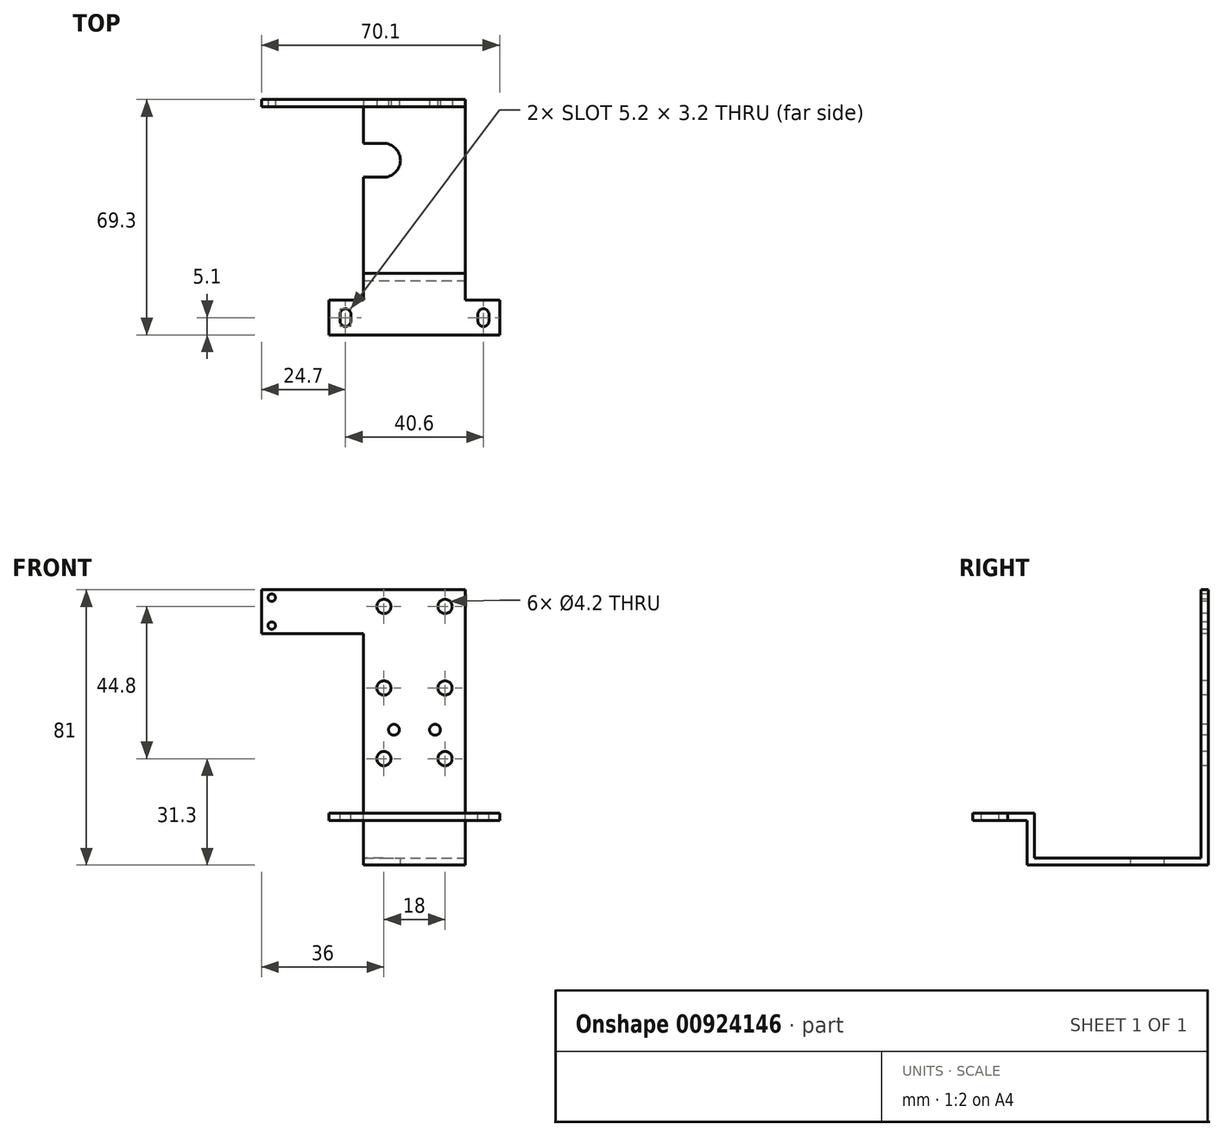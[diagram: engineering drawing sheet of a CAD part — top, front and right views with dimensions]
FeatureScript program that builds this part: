
annotation { "Feature Type Name" : "Feature", "Feature Type Description" : "" }
export const myFeature = defineFeature(function(context is Context, id is Id, definition is map)
    precondition{}
    {
        {
            var Q0;
            Q0=qCreatedBy(makeId("Front.planeOp"),FACE);
            var sketch = newSketch(context, id + "F0", { "sketchPlane" : qUnion([Q0])});
            skLineSegment(sketch, "E0.bottom", {"start": v(15, -40.5) * mm, "end": v(-15, -40.5) * mm});
            skLineSegment(sketch, "E0.top", {"start": v(15, 40.5) * mm, "end": v(-15, 40.5) * mm});
            skLineSegment(sketch, "E0.left", {"start": v(15, -40.5) * mm, "end": v(15, 40.5) * mm});
            skLineSegment(sketch, "E0.right", {"start": v(-15, -40.5) * mm, "end": v(-15, 40.5) * mm});
            skPoint(sketch, "E0.middle", {"position": v(0, 0) * mm});
            skSolve(sketch);
        }
        {
            var Q0;
            Q0=qSketchRegion(id+"F0",true);
            extrude(context, id + "F1", {"entities" : qUnion([Q0]), "offsetDistance" : 25 * mm, "depth" : 2.1 * mm});
        }
        {
            var Q0;
            Q0=makeQuery(id+"F1.opExtrude","CAP_FACE",FACE,{"disambiguationData":[OSD([sQuery(id+"F0.wireOp",EDGE,"E0.bottom"),sQuery(id+"F0.wireOp",EDGE,"E0.top"),sQuery(id+"F0.wireOp",EDGE,"E0.left"),sQuery(id+"F0.wireOp",EDGE,"E0.right")])],"isStart":false});
            var sketch = newSketch(context, id + "F2", { "sketchPlane" : qUnion([Q0])});
            skLineSegment(sketch, "E1.bottom", {"start": v(-15, -40.5) * mm, "end": v(15, -40.5) * mm});
            skLineSegment(sketch, "E1.top", {"start": v(-15, -38.4) * mm, "end": v(15, -38.4) * mm});
            skLineSegment(sketch, "E1.left", {"start": v(-15, -40.5) * mm, "end": v(-15, -38.4) * mm});
            skLineSegment(sketch, "E1.right", {"start": v(15, -40.5) * mm, "end": v(15, -38.4) * mm});
            skSolve(sketch);
        }
        {
            var Q0;
            Q0=qSketchRegion(id+"F2",true);
            extrude(context, id + "F3", {"entities" : qUnion([Q0]), "operationType" : NewBodyOperationType.ADD, "depth" : 51.2 * mm});
        }
        {
            var Q0;
            Q0=makeQuery(id+"F3.opExtrude","SWEPT_FACE",FACE,{"disambiguationData":[OSD([sQuery(id+"F2.wireOp",EDGE,"E1.top")])]});
            var sketch = newSketch(context, id + "F4", { "sketchPlane" : qUnion([Q0])});
            skLineSegment(sketch, "E2.bottom", {"start": v(-15, -53.3) * mm, "end": v(15, -53.3) * mm});
            skLineSegment(sketch, "E2.top", {"start": v(-15, -51.2) * mm, "end": v(15, -51.2) * mm});
            skLineSegment(sketch, "E2.left", {"start": v(-15, -53.3) * mm, "end": v(-15, -51.2) * mm});
            skLineSegment(sketch, "E2.right", {"start": v(15, -53.3) * mm, "end": v(15, -51.2) * mm});
            skSolve(sketch);
        }
        {
            var Q0;
            Q0=qSketchRegion(id+"F4",true);
            extrude(context, id + "F5", {"entities" : qUnion([Q0]), "operationType" : NewBodyOperationType.ADD, "depth" : 13.1 * mm});
        }
        {
            var Q0;
            Q0=makeQuery(id+"F5.boolean.opBoolean","MERGE",FACE,{"derivedFrom":[makeQuery(id+"F3.opExtrude","CAP_FACE",FACE,{"disambiguationData":[OSD([sQuery(id+"F2.wireOp",EDGE,"E1.bottom"),sQuery(id+"F2.wireOp",EDGE,"E1.top"),sQuery(id+"F2.wireOp",EDGE,"E1.left"),sQuery(id+"F2.wireOp",EDGE,"E1.right")])],"isStart":false}),makeQuery(id+"F5.opExtrude","SWEPT_FACE",FACE,{"disambiguationData":[OSD([sQuery(id+"F4.wireOp",EDGE,"E2.bottom")])]})]});
            var sketch = newSketch(context, id + "F6", { "sketchPlane" : qUnion([Q0])});
            skLineSegment(sketch, "E3.bottom", {"start": v(-15, -25.3) * mm, "end": v(15, -25.3) * mm});
            skLineSegment(sketch, "E3.top", {"start": v(-15, -27.4) * mm, "end": v(15, -27.4) * mm});
            skLineSegment(sketch, "E3.left", {"start": v(-15, -25.3) * mm, "end": v(-15, -27.4) * mm});
            skLineSegment(sketch, "E3.right", {"start": v(15, -25.3) * mm, "end": v(15, -27.4) * mm});
            skSolve(sketch);
        }
        {
            var Q0;
            Q0=qSketchRegion(id+"F6",true);
            extrude(context, id + "F7", {"entities" : qUnion([Q0]), "operationType" : NewBodyOperationType.ADD, "depth" : 16 * mm});
        }
        {
            var Q0;
            Q0=makeQuery(id+"F7.boolean.opBoolean","MERGE",FACE,{"derivedFrom":[makeQuery(id+"F5.opExtrude","CAP_FACE",FACE,{"disambiguationData":[OSD([sQuery(id+"F4.wireOp",EDGE,"E2.bottom"),sQuery(id+"F4.wireOp",EDGE,"E2.top"),sQuery(id+"F4.wireOp",EDGE,"E2.left"),sQuery(id+"F4.wireOp",EDGE,"E2.right")])],"isStart":false}),makeQuery(id+"F7.opExtrude","SWEPT_FACE",FACE,{"disambiguationData":[OSD([sQuery(id+"F6.wireOp",EDGE,"E3.bottom")])]})]});
            var sketch = newSketch(context, id + "F8", { "sketchPlane" : qUnion([Q0])});
            skLineSegment(sketch, "E4.bottom", {"start": v(-25.1, -69.3) * mm, "end": v(25.1, -69.3) * mm});
            skLineSegment(sketch, "E4.top", {"start": v(-25.1, -59.1) * mm, "end": v(25.1, -59.1) * mm});
            skLineSegment(sketch, "E4.left", {"start": v(-25.1, -69.3) * mm, "end": v(-25.1, -59.1) * mm});
            skLineSegment(sketch, "E4.right", {"start": v(25.1, -69.3) * mm, "end": v(25.1, -59.1) * mm});
            skLineSegment(sketch, "E5", {"start": v(0, -51.2) * mm, "end": v(0, -65.26) * mm});
            skSolve(sketch);
        }
        {
            var Q0;
            {var subQ3=sQuery(id+"F8.wireOp",EDGE,"E4.left");Q0=makeQuery(id+"F8.imprint","IMPRINT",FACE,{"disambiguationData":[TD([[makeQuery(id+"F8.imprint","IMPRINT",EDGE,{"derivedFrom":subQ3}),-1.0]])]});}
            var Q1;
            {var subQ3=sQuery(id+"F8.wireOp",EDGE,"E4.right");Q1=makeQuery(id+"F8.imprint","IMPRINT",FACE,{"disambiguationData":[TD([[makeQuery(id+"F8.imprint","IMPRINT",EDGE,{"derivedFrom":subQ3}),1.0]])]});}
            extrude(context, id + "F9", {"entities" : qUnion([Q0, Q1]), "operationType" : NewBodyOperationType.ADD, "oppositeDirection" : true, "depth" : 2.1 * mm});
        }
        {
            var Q0;
            {var subQ0=sQuery(id+"F8.wireOp",EDGE,"E4.top");var subQ1=sQuery(id+"F8.wireOp",EDGE,"E4.bottom");var subQ2=sQuery(id+"F6.wireOp",EDGE,"E3.bottom");var subQ3=sQuery(id+"F4.wireOp",EDGE,"E2.right");var subQ4=sQuery(id+"F4.wireOp",EDGE,"E2.left");Q0=makeQuery(id+"F9.boolean.opBoolean","MERGE",FACE,{"derivedFrom":[makeQuery(id+"F7.boolean.opBoolean","MERGE",FACE,{"derivedFrom":[makeQuery(id+"F5.opExtrude","CAP_FACE",FACE,{"disambiguationData":[OSD([sQuery(id+"F4.wireOp",EDGE,"E2.bottom"),sQuery(id+"F4.wireOp",EDGE,"E2.top"),subQ4,subQ3])],"isStart":false}),makeQuery(id+"F7.opExtrude","SWEPT_FACE",FACE,{"disambiguationData":[OSD([subQ2])]})]}),makeQuery(id+"F9.opExtrude","CAP_FACE",FACE,{"disambiguationData":[OSD([subQ4,subQ2,sQuery(id+"F6.wireOp",EDGE,"E3.left"),subQ1,subQ0,sQuery(id+"F8.wireOp",EDGE,"E4.left")])],"isStart":true}),makeQuery(id+"F9.opExtrude","CAP_FACE",FACE,{"disambiguationData":[OSD([subQ3,subQ2,sQuery(id+"F6.wireOp",EDGE,"E3.right"),subQ1,subQ0,sQuery(id+"F8.wireOp",EDGE,"E4.right")])],"isStart":true})]});}
            var sketch = newSketch(context, id + "F10", { "sketchPlane" : qUnion([Q0])});
            skArc(sketch, "E6", {"start": v(-21.9, -65.2) * mm, "mid": v(-20.3, -66.8) * mm, "end": v(-18.7, -65.2) * mm});
            skArc(sketch, "E7", {"start": v(-18.7, -63.2) * mm, "mid": v(-20.3, -61.6) * mm, "end": v(-21.9, -63.2) * mm});
            skLineSegment(sketch, "E8", {"start": v(-21.9, -63.2) * mm, "end": v(-21.9, -65.2) * mm});
            skLineSegment(sketch, "E9", {"start": v(-18.7, -65.2) * mm, "end": v(-18.7, -63.2) * mm});
            skLineSegment(sketch, "E10", {"start": v(-20.3, -63.2) * mm, "end": v(-20.3, -65.2) * mm});
            skPoint(sketch, "E11", {"position": v(-20.3, -64.2) * mm});
            skLineSegment(sketch, "E12", {"start": v(0, -69.3) * mm, "end": v(0, -51.2) * mm});
            skLineSegment(sketch, "E13.MirrorCS", {"start": v(18.7, -65.2) * mm, "end": v(18.7, -63.2) * mm});
            skArc(sketch, "E14.MirrorCS", {"start": v(18.7, -63.2) * mm, "mid": v(20.3, -61.6) * mm, "end": v(21.9, -63.2) * mm});
            skLineSegment(sketch, "E15.MirrorCS", {"start": v(21.9, -63.2) * mm, "end": v(21.9, -65.2) * mm});
            skArc(sketch, "E16.MirrorCS", {"start": v(21.9, -65.2) * mm, "mid": v(20.3, -66.8) * mm, "end": v(18.7, -65.2) * mm});
            skSolve(sketch);
        }
        {
            var Q0;
            Q0=makeQuery(id+"F10.imprint","IMPRINT",FACE,{"disambiguationData":[TD([[makeQuery(id+"F10.imprint","IMPRINT",EDGE,{"derivedFrom":sQuery(id+"F10.wireOp",EDGE,"E6")}),1.0]])]});
            var Q1;
            Q1=makeQuery(id+"F10.imprint","IMPRINT",FACE,{"disambiguationData":[TD([[makeQuery(id+"F10.imprint","IMPRINT",EDGE,{"derivedFrom":sQuery(id+"F10.wireOp",EDGE,"E13.MirrorCS")}),-1.0]])]});
            extrude(context, id + "F11", {"entities" : qUnion([Q0, Q1]), "operationType" : NewBodyOperationType.REMOVE, "endBound" : BoundingType.THROUGH_ALL, "oppositeDirection" : true, "depth" : 25 * mm});
        }
        {
            var Q0;
            Q0=makeQuery(id+"F3.opExtrude","SWEPT_FACE",FACE,{"disambiguationData":[OSD([sQuery(id+"F2.wireOp",EDGE,"E1.top")])]});
            var sketch = newSketch(context, id + "F12", { "sketchPlane" : qUnion([Q0])});
            skArc(sketch, "E17", {"start": v(-9.15, -22.9) * mm, "mid": v(-4.15, -17.9) * mm, "end": v(-9.15, -12.9) * mm});
            skLineSegment(sketch, "E18", {"start": v(-9.15, -12.9) * mm, "end": v(-15, -12.9) * mm});
            skLineSegment(sketch, "E19", {"start": v(-9.15, -22.9) * mm, "end": v(-15, -22.9) * mm});
            skLineSegment(sketch, "E20", {"start": v(-15, -22.9) * mm, "end": v(-15, -12.9) * mm});
            skSolve(sketch);
        }
        {
            var Q0;
            Q0=qSketchRegion(id+"F12",true);
            extrude(context, id + "F13", {"entities" : qUnion([Q0]), "operationType" : NewBodyOperationType.REMOVE, "endBound" : BoundingType.THROUGH_ALL, "oppositeDirection" : true, "depth" : 25 * mm});
        }
        {
            var Q0;
            Q0=makeQuery(id+"F1.opExtrude","CAP_FACE",FACE,{"disambiguationData":[OSD([sQuery(id+"F0.wireOp",EDGE,"E0.bottom"),sQuery(id+"F0.wireOp",EDGE,"E0.top"),sQuery(id+"F0.wireOp",EDGE,"E0.left"),sQuery(id+"F0.wireOp",EDGE,"E0.right")])],"isStart":false});
            var sketch = newSketch(context, id + "F14", { "sketchPlane" : qUnion([Q0])});
            skCircle(sketch, "E21", {"center": v(9, 35.6) * mm, "radius": 2.1 * mm});
            skCircle(sketch, "E22.0.1.0", {"center": v(9, 11.6) * mm, "radius": 2.1 * mm});
            skCircle(sketch, "E22.1.0.0", {"center": v(-9, 35.6) * mm, "radius": 2.1 * mm});
            skCircle(sketch, "E22.1.1.0", {"center": v(-9, 11.6) * mm, "radius": 2.1 * mm});
            skLineSegment(sketch, "E22.direction1", {"start": v(9, 35.6) * mm, "end": v(-9, 35.6) * mm, "construction": true});
            skLineSegment(sketch, "E22.direction2", {"start": v(9, 35.6) * mm, "end": v(9, 11.6) * mm, "construction": true});
            skCircle(sketch, "E23", {"center": v(9, -9.2) * mm, "radius": 2.1 * mm});
            skCircle(sketch, "E24.1.0.0", {"center": v(-9, -9.2) * mm, "radius": 2.1 * mm});
            skLineSegment(sketch, "E24.direction1", {"start": v(9, -9.2) * mm, "end": v(-9, -9.2) * mm, "construction": true});
            skCircle(sketch, "E25", {"center": v(6.05, -0.7) * mm, "radius": 1.6 * mm});
            skCircle(sketch, "E26", {"center": v(-6.05, -0.7) * mm, "radius": 1.6 * mm});
            skSolve(sketch);
        }
        {
            var Q0;
            Q0=qSketchRegion(id+"F14",true);
            extrude(context, id + "F15", {"entities" : qUnion([Q0]), "operationType" : NewBodyOperationType.REMOVE, "endBound" : BoundingType.THROUGH_ALL, "oppositeDirection" : true, "depth" : 25 * mm});
        }
        {
            var Q0;
            {var subQ0=sQuery(id+"F0.wireOp",EDGE,"E0.top");var subQ1=sQuery(id+"F0.wireOp",EDGE,"E0.right");Q0=makeQuery(id+"F13.boolean.opBoolean","SPLIT",FACE,{"disambiguationData":[TD([makeQuery(id+"F1.opExtrude","SWEPT_FACE",FACE,{"disambiguationData":[OSD([subQ0])]})])],"derivedFrom":makeQuery(id+"F7.boolean.opBoolean","MERGE",FACE,{"derivedFrom":[makeQuery(id+"F5.boolean.opBoolean","MERGE",FACE,{"derivedFrom":[makeQuery(id+"F3.boolean.opBoolean","MERGE",FACE,{"derivedFrom":[makeQuery(id+"F1.opExtrude","SWEPT_FACE",FACE,{"disambiguationData":[OSD([subQ1])]}),makeQuery(id+"F3.opExtrude","SWEPT_FACE",FACE,{"disambiguationData":[OSD([sQuery(id+"F2.wireOp",EDGE,"E1.left")])]})]}),makeQuery(id+"F5.opExtrude","SWEPT_FACE",FACE,{"disambiguationData":[OSD([sQuery(id+"F4.wireOp",EDGE,"E2.left")])]})]}),makeQuery(id+"F7.opExtrude","SWEPT_FACE",FACE,{"disambiguationData":[OSD([sQuery(id+"F6.wireOp",EDGE,"E3.left")])]})]})});}
            var sketch = newSketch(context, id + "F16", { "sketchPlane" : qUnion([Q0])});
            skLineSegment(sketch, "E27.bottom", {"start": v(0, 40.5) * mm, "end": v(2.1, 40.5) * mm});
            skLineSegment(sketch, "E27.top", {"start": v(0, 27.65) * mm, "end": v(2.1, 27.65) * mm});
            skLineSegment(sketch, "E27.left", {"start": v(0, 40.5) * mm, "end": v(0, 27.65) * mm});
            skLineSegment(sketch, "E27.right", {"start": v(2.1, 40.5) * mm, "end": v(2.1, 27.65) * mm});
            skSolve(sketch);
        }
        {
            var Q0;
            Q0=qSketchRegion(id+"F16",true);
            extrude(context, id + "F17", {"entities" : qUnion([Q0]), "operationType" : NewBodyOperationType.ADD, "depth" : 30 * mm, "offsetDistance" : 25 * mm});
        }
        {
            var Q0;
            Q0=makeQuery(id+"F17.boolean.opBoolean","MERGE",FACE,{"derivedFrom":[makeQuery(id+"F1.opExtrude","CAP_FACE",FACE,{"disambiguationData":[OSD([sQuery(id+"F0.wireOp",EDGE,"E0.bottom"),sQuery(id+"F0.wireOp",EDGE,"E0.top"),sQuery(id+"F0.wireOp",EDGE,"E0.left"),sQuery(id+"F0.wireOp",EDGE,"E0.right")])],"isStart":false}),makeQuery(id+"F17.opExtrude","SWEPT_FACE",FACE,{"disambiguationData":[OSD([sQuery(id+"F16.wireOp",EDGE,"E27.right")])]})]});
            var sketch = newSketch(context, id + "F18", { "sketchPlane" : qUnion([Q0])});
            skCircle(sketch, "E28", {"center": v(-42, 38.17) * mm, "radius": 1.1 * mm});
            skCircle(sketch, "E29", {"center": v(-42, 29.97) * mm, "radius": 1.1 * mm});
            skLineSegment(sketch, "E30", {"start": v(-45, 34.08) * mm, "end": v(-26.44, 34.08) * mm});
            skSolve(sketch);
        }
        {
            var Q0;
            Q0=makeQuery(id+"F18.imprint","IMPRINT",FACE,{"disambiguationData":[TD([[makeQuery(id+"F18.imprint","IMPRINT",EDGE,{"derivedFrom":sQuery(id+"F18.wireOp",EDGE,"E28")}),1.0]])]});
            var Q1;
            Q1=makeQuery(id+"F18.imprint","IMPRINT",FACE,{"disambiguationData":[TD([[makeQuery(id+"F18.imprint","IMPRINT",EDGE,{"derivedFrom":sQuery(id+"F18.wireOp",EDGE,"E29")}),1.0]])]});
            extrude(context, id + "F19", {"entities" : qUnion([Q0, Q1]), "operationType" : NewBodyOperationType.REMOVE, "oppositeDirection" : true, "depth" : 25 * mm, "offsetDistance" : 25 * mm});
        }
    });
